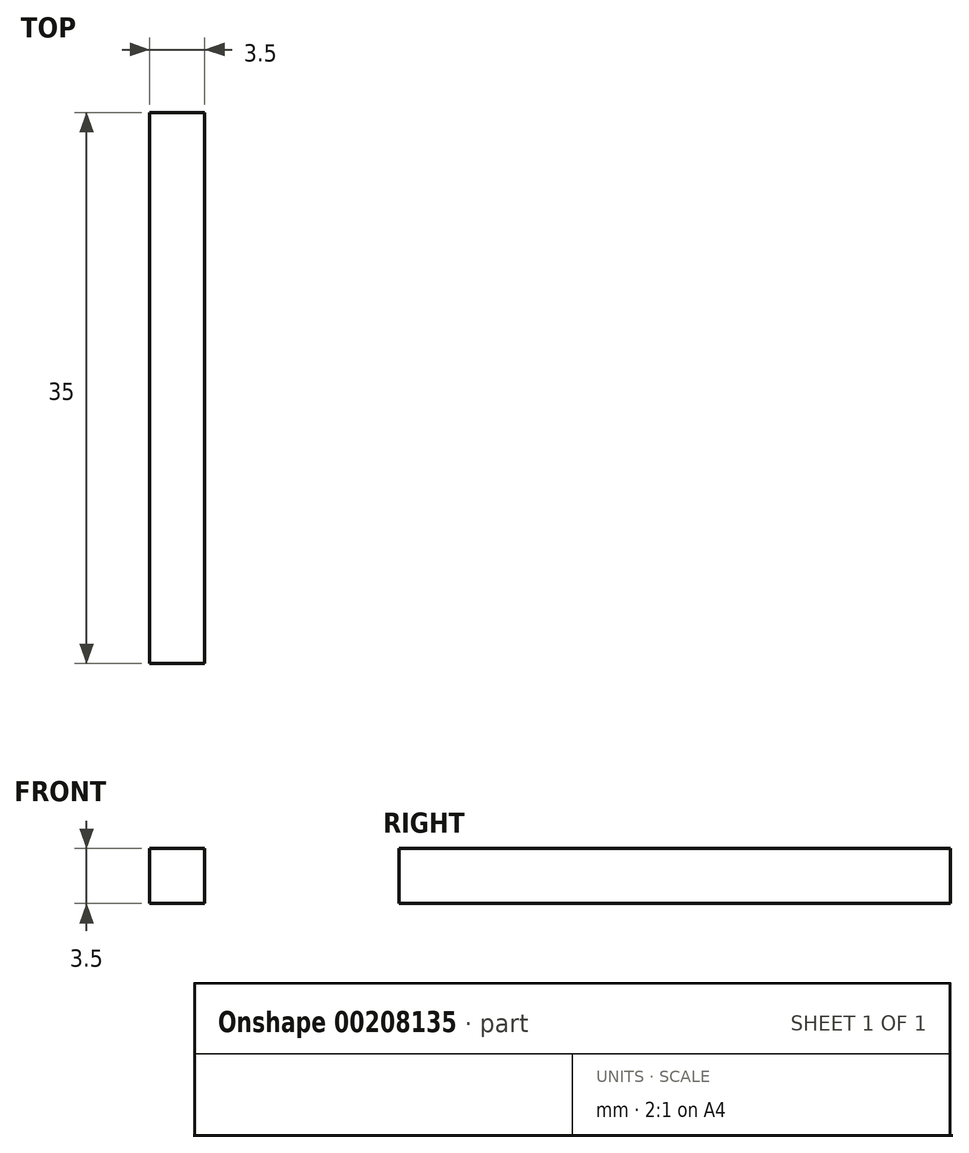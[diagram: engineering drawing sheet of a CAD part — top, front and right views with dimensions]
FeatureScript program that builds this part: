
annotation { "Feature Type Name" : "Feature", "Feature Type Description" : "" }
export const myFeature = defineFeature(function(context is Context, id is Id, definition is map)
    precondition{}
    {
        {
            var Q0;
            Q0=qCreatedBy(makeId("Top.planeOp"),FACE);
            var sketch = newSketch(context, id + "F0", { "sketchPlane" : qUnion([Q0])});
            skLineSegment(sketch, "E0.bottom", {"start": v(1.75, -17.5) * mm, "end": v(-1.75, -17.5) * mm});
            skLineSegment(sketch, "E0.top", {"start": v(1.75, 17.5) * mm, "end": v(-1.75, 17.5) * mm});
            skLineSegment(sketch, "E0.left", {"start": v(1.75, -17.5) * mm, "end": v(1.75, 17.5) * mm});
            skLineSegment(sketch, "E0.right", {"start": v(-1.75, -17.5) * mm, "end": v(-1.75, 17.5) * mm});
            skPoint(sketch, "E0.middle", {"position": v(0, 0) * mm});
            skSolve(sketch);
        }
        {
            var Q0;
            Q0 = qSketchRegion(id + "F0", true);
            extrude(context, id + "F1", {"entities" : qUnion([Q0]), "depth" : 3.5 * mm});
        }
    });
